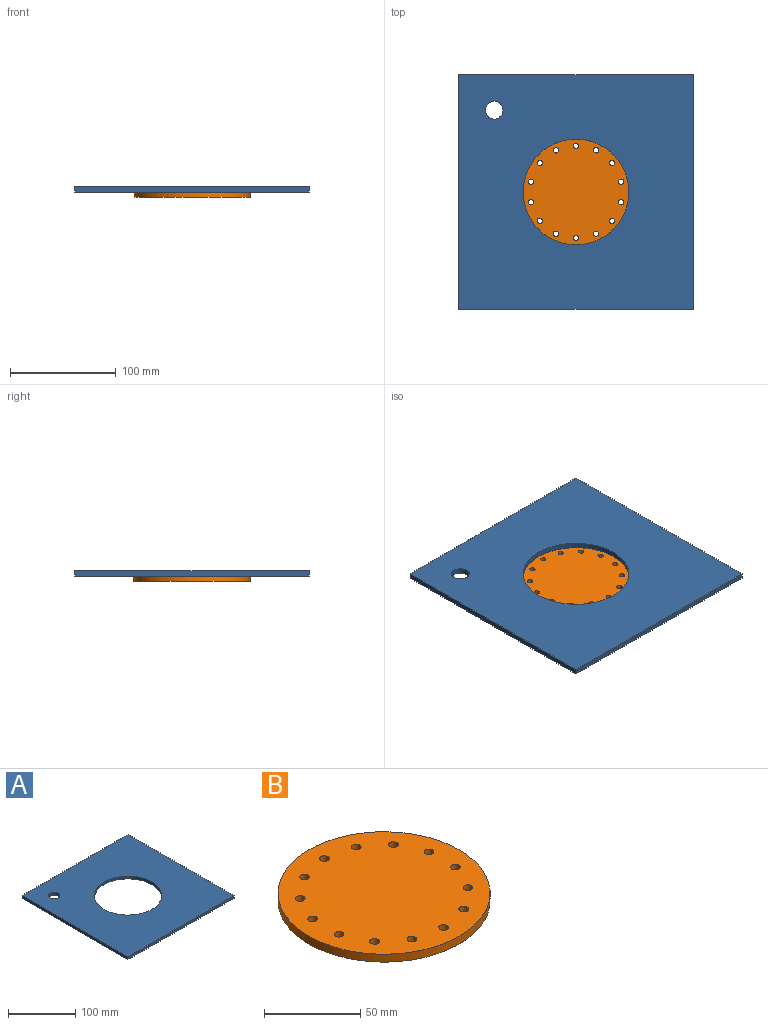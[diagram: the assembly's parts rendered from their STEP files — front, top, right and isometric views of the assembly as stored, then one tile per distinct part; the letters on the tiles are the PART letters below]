
ASSEMBLY  parts=2 mates=1
PART A: 8 faces, bbox 222.3x222.3x5 mm
  f0: plane 222.25x5mm, normal (0,-1,0), area 1111.2mm2, adj f1,f3,f4,f5
  f1: plane 222.25x5mm, normal (1,0,0), area 1111.2mm2, adj f0,f2,f4,f5
  f2: plane 222.25x5mm, normal (0,1,0), area 1111.2mm2, adj f1,f3,f4,f5
  f3: plane 222.25x5mm, normal (-1,0,0), area 1111.2mm2, adj f0,f2,f4,f5
  f4: plane 222.25x222.25mm, normal (0,0,1), area 41322.9mm2, adj f0,f1,f2,f3,f6,f7
  f5: plane 222.25x222.25mm, normal (0,0,-1), area 41322.9mm2, adj f0,f1,f2,f3,f6,f7
  f6: cylinder r=50mm len=100mm, axis (0,0,1), area 1570.8mm2, adj f4,f5
  f7: cylinder r=8.33mm len=16.67mm, axis (0,0,1), area 261.8mm2, adj f4,f5
PART B: 17 faces, bbox 110x110x5 mm
  f0: cylinder r=55mm len=110mm, axis (0,0,-1), area 1727.9mm2, adj f1,f2
  f1: plane 110x110mm, normal (0,0,1), area 9228.4mm2, adj f0,f3,f4,f5,f6,f7,f8,f9
  f2: plane 110x110mm, normal (0,0,-1), area 9228.4mm2, adj f0,f3,f4,f5,f6,f7,f8,f9
  f3: cylinder r=2.5mm len=5mm, axis (0,0,1), area 78.5mm2, adj f1,f2
  f4: cylinder r=2.5mm len=5mm, axis (0,0,1), area 78.5mm2, adj f1,f2
  f5: cylinder r=2.5mm len=5mm, axis (0,0,1), area 78.5mm2, adj f1,f2
  f6: cylinder r=2.5mm len=5mm, axis (0,0,1), area 78.5mm2, adj f1,f2
  f7: cylinder r=2.5mm len=5mm, axis (0,0,1), area 78.5mm2, adj f1,f2
  f8: cylinder r=2.5mm len=5mm, axis (0,0,1), area 78.5mm2, adj f1,f2
  f9: cylinder r=2.5mm len=5mm, axis (0,0,1), area 78.5mm2, adj f1,f2
  f10: cylinder r=2.5mm len=5mm, axis (0,0,1), area 78.5mm2, adj f1,f2
  f11: cylinder r=2.5mm len=5mm, axis (0,0,1), area 78.5mm2, adj f1,f2
  f12: cylinder r=2.5mm len=5mm, axis (0,0,1), area 78.5mm2, adj f1,f2
  f13: cylinder r=2.5mm len=5mm, axis (0,0,1), area 78.5mm2, adj f1,f2
  f14: cylinder r=2.5mm len=5mm, axis (0,0,1), area 78.5mm2, adj f1,f2
  f15: cylinder r=2.5mm len=5mm, axis (0,0,1), area 78.5mm2, adj f1,f2
  f16: cylinder r=2.5mm len=5mm, axis (0,0,1), area 78.5mm2, adj f1,f2
PLACE A at identity
PLACE B t=(0,0,-5)mm
MATE parallel B.f0 <-> A.f5  axis (0,0,1) through (0,0,0)mm
